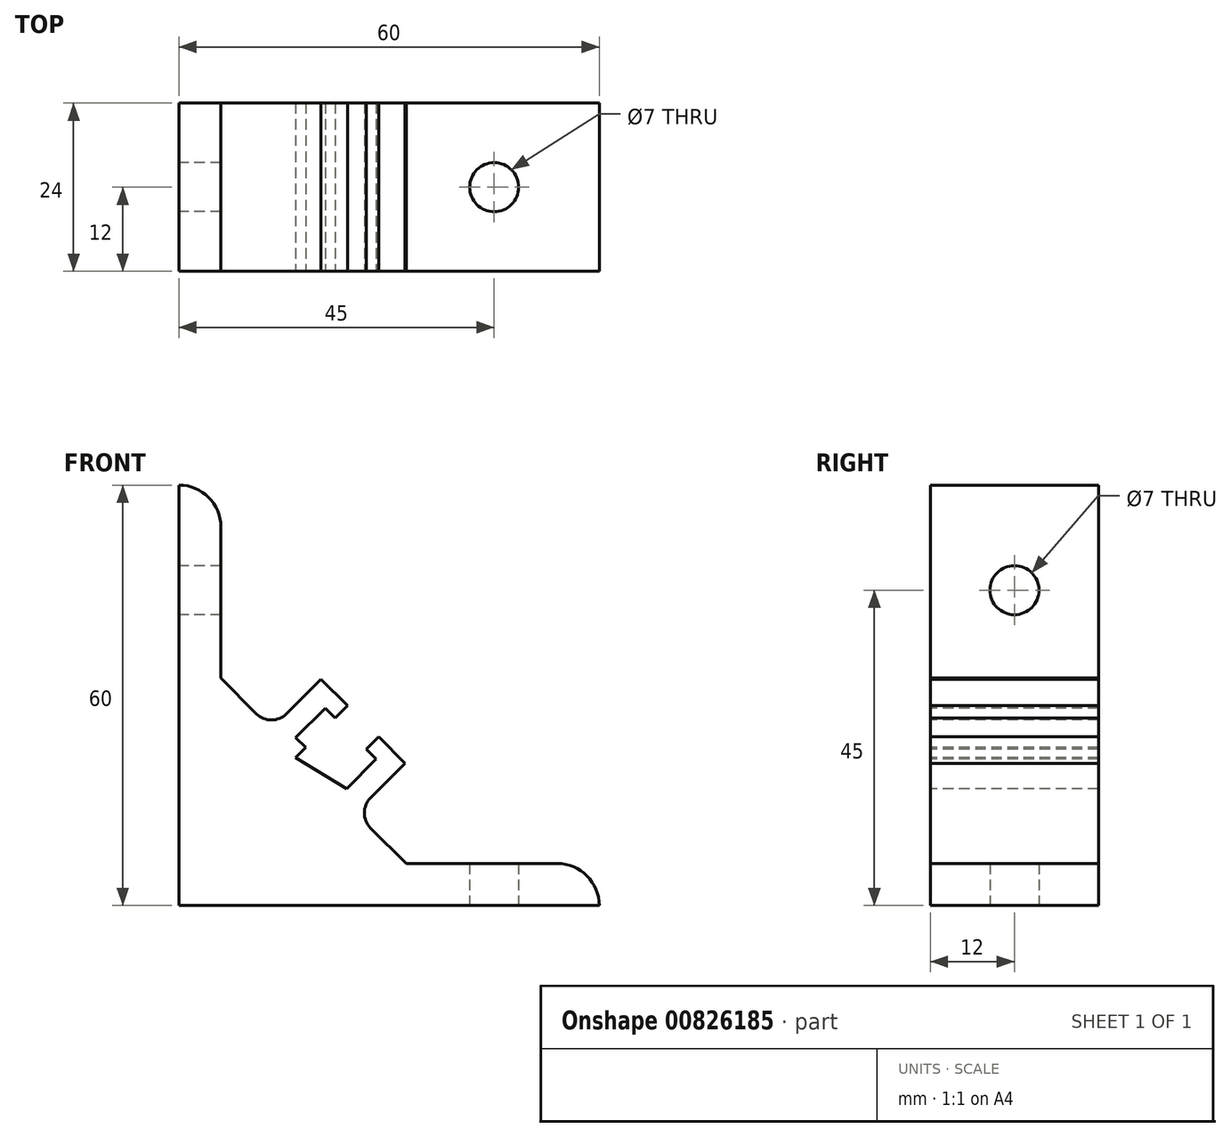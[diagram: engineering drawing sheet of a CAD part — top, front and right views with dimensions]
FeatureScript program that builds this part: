
annotation { "Feature Type Name" : "Feature", "Feature Type Description" : "" }
export const myFeature = defineFeature(function(context is Context, id is Id, definition is map)
    precondition{}
    {
        {
            var Q0;
            Q0=qCreatedBy(makeId("Front.planeOp"),FACE);
            var sketch = newSketch(context, id + "F0", { "sketchPlane" : qUnion([Q0])});
            skLineSegment(sketch, "E0", {"start": v(0, 60) * mm, "end": v(0, 0) * mm});
            skLineSegment(sketch, "E1", {"start": v(0, 0) * mm, "end": v(60, 0) * mm});
            skArc(sketch, "E2", {"start": v(4, 4.5) * mm, "mid": v(4.15, 4.15) * mm, "end": v(4.5, 4) * mm});
            skLineSegment(sketch, "E3", {"start": v(4.5, 4) * mm, "end": v(29, 4) * mm});
            skArc(sketch, "E4", {"start": v(29, 4) * mm, "mid": v(29.46, 4.3) * mm, "end": v(29.35, 4.85) * mm});
            skLineSegment(sketch, "E5", {"start": v(4, 29) * mm, "end": v(4, 4.5) * mm});
            skArc(sketch, "E6", {"start": v(4.85, 29.35) * mm, "mid": v(4.3, 29.46) * mm, "end": v(4, 29) * mm});
            skLineSegment(sketch, "E7", {"start": v(4.85, 29.35) * mm, "end": v(13.57, 20.64) * mm});
            skLineSegment(sketch, "E8", {"start": v(20.64, 13.57) * mm, "end": v(29.35, 4.85) * mm});
            skLineSegment(sketch, "E9", {"start": v(54, 6) * mm, "end": v(32.45, 6) * mm});
            skArc(sketch, "E10", {"start": v(60, 0) * mm, "mid": v(58.24, 4.24) * mm, "end": v(54, 6) * mm});
            skLineSegment(sketch, "E11", {"start": v(6, 54) * mm, "end": v(6, 32.45) * mm});
            skArc(sketch, "E12", {"start": v(6, 54) * mm, "mid": v(4.24, 58.24) * mm, "end": v(0, 60) * mm});
            skLineSegment(sketch, "E13", {"start": v(27.36, 11.1) * mm, "end": v(32.45, 6) * mm});
            skArc(sketch, "E14", {"start": v(27.36, 15.34) * mm, "mid": v(26.48, 13.21) * mm, "end": v(27.36, 11.1) * mm});
            skLineSegment(sketch, "E15", {"start": v(6, 32.45) * mm, "end": v(11.1, 27.36) * mm});
            skArc(sketch, "E16", {"start": v(11.1, 27.36) * mm, "mid": v(13.21, 26.48) * mm, "end": v(15.34, 27.36) * mm});
            skLineSegment(sketch, "E17", {"start": v(24.07, 28.52) * mm, "end": v(20.29, 32.3) * mm});
            skLineSegment(sketch, "E18", {"start": v(15.34, 27.36) * mm, "end": v(20.29, 32.3) * mm});
            skLineSegment(sketch, "E19", {"start": v(28.52, 24.07) * mm, "end": v(32.3, 20.29) * mm});
            skLineSegment(sketch, "E20", {"start": v(27.36, 15.34) * mm, "end": v(32.3, 20.29) * mm});
            skLineSegment(sketch, "E21", {"start": v(28.52, 24.07) * mm, "end": v(26.76, 22.3) * mm});
            skLineSegment(sketch, "E22", {"start": v(28.17, 20.89) * mm, "end": v(23.96, 16.68) * mm});
            skLineSegment(sketch, "E23", {"start": v(26.76, 22.3) * mm, "end": v(28.17, 20.89) * mm});
            skLineSegment(sketch, "E24", {"start": v(24.07, 28.52) * mm, "end": v(22.3, 26.76) * mm});
            skLineSegment(sketch, "E25", {"start": v(22.3, 26.76) * mm, "end": v(20.89, 28.17) * mm});
            skLineSegment(sketch, "E26", {"start": v(20.89, 28.17) * mm, "end": v(16.68, 23.96) * mm});
            skLineSegment(sketch, "E27", {"start": v(16.64, 21.1) * mm, "end": v(18.1, 22.55) * mm});
            skLineSegment(sketch, "E28", {"start": v(16.68, 23.96) * mm, "end": v(18.1, 22.55) * mm});
            skLineSegment(sketch, "E29", {"start": v(16.64, 21.1) * mm, "end": v(23.96, 16.68) * mm});
            skLineSegment(sketch, "E30", {"start": v(45, -1.83) * mm, "end": v(45, 8.9) * mm});
            skLineSegment(sketch, "E31", {"start": v(-1.23, 45) * mm, "end": v(8.9, 45) * mm});
            skArc(sketch, "E32", {"start": v(15.83, 9.9) * mm, "mid": v(17.17, 10.39) * mm, "end": v(18.31, 11.24) * mm});
            skArc(sketch, "E33", {"start": v(11.24, 18.32) * mm, "mid": v(10.39, 17.17) * mm, "end": v(9.9, 15.83) * mm});
            skLineSegment(sketch, "E34", {"start": v(12.36, 14.13) * mm, "end": v(11.75, 13.97) * mm});
            skLineSegment(sketch, "E35", {"start": v(14.13, 12.36) * mm, "end": v(13.97, 11.75) * mm});
            skArc(sketch, "E36", {"start": v(14.13, 12.36) * mm, "mid": v(16.55, 16.55) * mm, "end": v(12.36, 14.13) * mm});
            skLineSegment(sketch, "E37", {"start": v(15.83, 9.9) * mm, "end": v(13.97, 11.75) * mm});
            skLineSegment(sketch, "E38", {"start": v(20.64, 13.57) * mm, "end": v(18.31, 11.24) * mm});
            skLineSegment(sketch, "E39", {"start": v(9.9, 15.83) * mm, "end": v(11.75, 13.97) * mm});
            skLineSegment(sketch, "E40", {"start": v(13.57, 20.64) * mm, "end": v(11.24, 18.32) * mm});
            skSolve(sketch);
        }
        {
            var Q0;
            {var subQ0=sQuery(id+"F0.wireOp",EDGE,"E12");Q0=makeQuery(id+"F0.imprint","IMPRINT",FACE,{"disambiguationData":[TD([[makeQuery(id+"F0.imprint","IMPRINT",EDGE,{"derivedFrom":subQ0}),1.0]])]});}
            var Q1;
            {var subQ0=sQuery(id+"F0.wireOp",EDGE,"E10");Q1=makeQuery(id+"F0.imprint","IMPRINT",FACE,{"disambiguationData":[TD([[makeQuery(id+"F0.imprint","IMPRINT",EDGE,{"derivedFrom":subQ0}),1.0]])]});}
            var Q2;
            Q2=makeQuery(id+"F0.imprint","IMPRINT",FACE,{"disambiguationData":[TD([[makeQuery(id+"F0.imprint","IMPRINT",EDGE,{"derivedFrom":sQuery(id+"F0.wireOp",EDGE,"E2")}),1.0]])]});
            var Q3;
            Q3=makeQuery(id+"F0.imprint","IMPRINT",FACE,{"disambiguationData":[TD([[makeQuery(id+"F0.imprint","IMPRINT",EDGE,{"derivedFrom":sQuery(id+"F0.wireOp",EDGE,"E2")}),-1.0]])]});
            extrude(context, id + "F1", {"entities" : qUnion([Q0, Q1, Q2, Q3]), "oppositeDirection" : true, "depth" : 24 * mm, "offsetDistance" : 25 * mm});
        }
        {
            var Q0;
            Q0=makeQuery(id+"F1.opExtrude","SWEPT_FACE",FACE,{"disambiguationData":[OSD([sQuery(id+"F0.wireOp",EDGE,"E0")])]});
            var sketch = newSketch(context, id + "F2", { "sketchPlane" : qUnion([Q0])});
            skCircle(sketch, "E41", {"center": v(-12, 45) * mm, "radius": 3.5 * mm});
            skSolve(sketch);
        }
        {
            var Q0;
            Q0=makeQuery(id+"F2.imprint","IMPRINT",FACE,{"disambiguationData":[TD([[makeQuery(id+"F2.imprint","IMPRINT",EDGE,{"derivedFrom":sQuery(id+"F2.wireOp",EDGE,"E41")}),1.0]])]});
            extrude(context, id + "F3", {"entities" : qUnion([Q0]), "operationType" : NewBodyOperationType.REMOVE, "oppositeDirection" : true, "depth" : 6 * mm, "offsetDistance" : 25 * mm});
        }
        {
            var Q0;
            Q0=makeQuery(id+"F1.opExtrude","SWEPT_FACE",FACE,{"disambiguationData":[OSD([sQuery(id+"F0.wireOp",EDGE,"E1")])]});
            var sketch = newSketch(context, id + "F4", { "sketchPlane" : qUnion([Q0])});
            skCircle(sketch, "E42", {"center": v(45, -12) * mm, "radius": 3.5 * mm});
            skSolve(sketch);
        }
        {
            var Q0;
            Q0=makeQuery(id+"F4.imprint","IMPRINT",FACE,{"disambiguationData":[TD([[makeQuery(id+"F4.imprint","IMPRINT",EDGE,{"derivedFrom":sQuery(id+"F4.wireOp",EDGE,"E42")}),1.0]])]});
            extrude(context, id + "F5", {"entities" : qUnion([Q0]), "operationType" : NewBodyOperationType.REMOVE, "oppositeDirection" : true, "depth" : 6 * mm, "offsetDistance" : 25 * mm});
        }
    });
